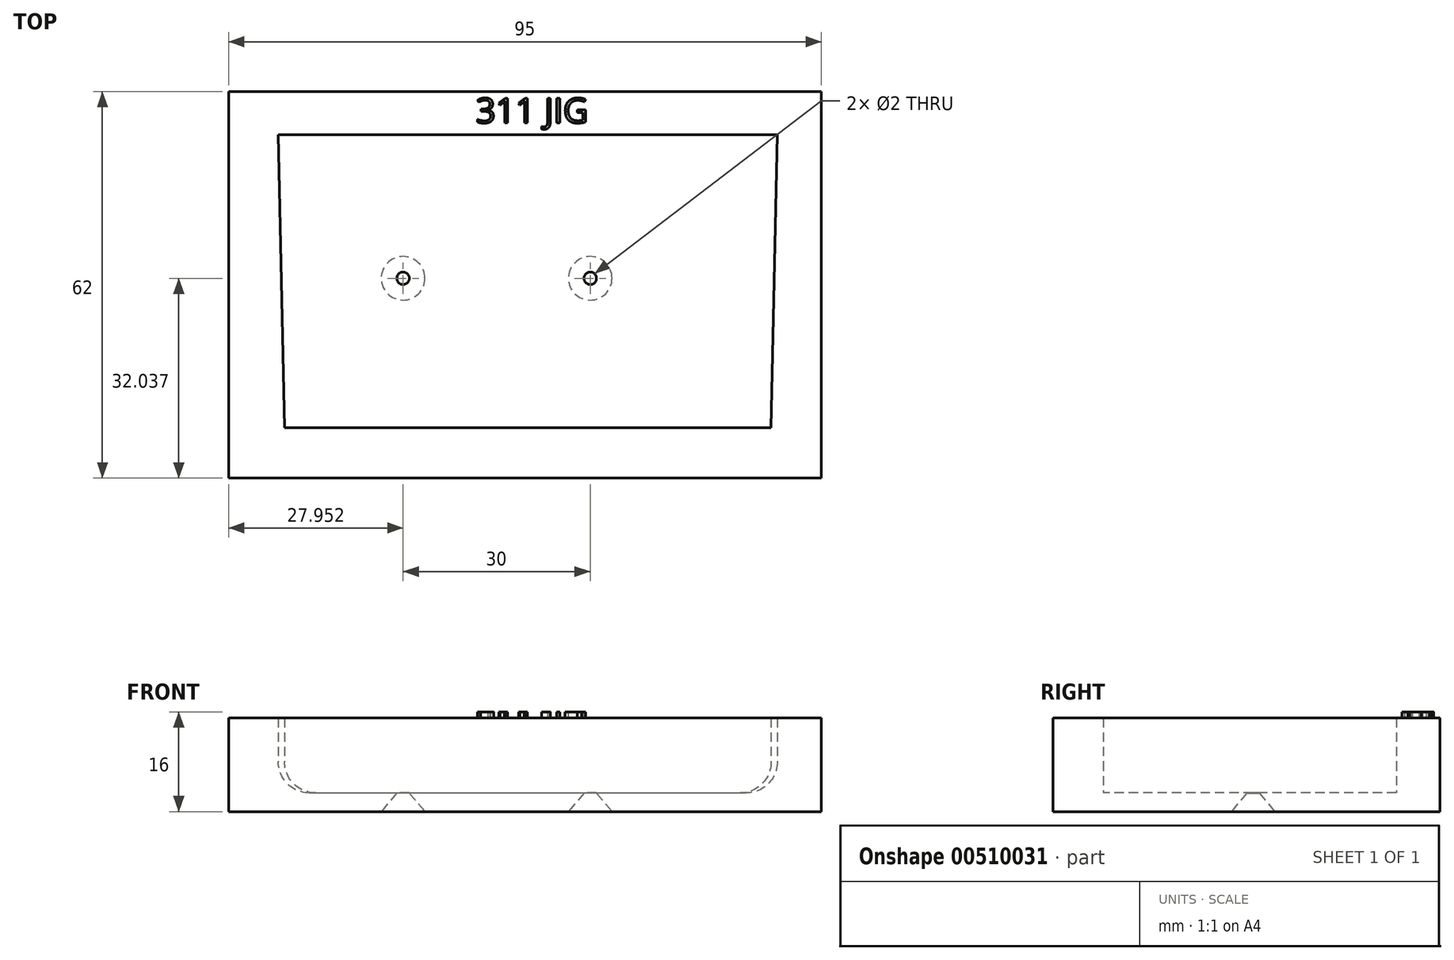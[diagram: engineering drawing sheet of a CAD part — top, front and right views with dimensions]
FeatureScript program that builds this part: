
annotation { "Feature Type Name" : "Feature", "Feature Type Description" : "" }
export const myFeature = defineFeature(function(context is Context, id is Id, definition is map)
    precondition{}
    {
        {
            var Q0;
            Q0=qCreatedBy(makeId("Top.planeOp"),FACE);
            var sketch = newSketch(context, id + "F0", { "sketchPlane" : qUnion([Q0])});
            skLineSegment(sketch, "E0.bottom", {"start": v(-47.5, 31) * mm, "end": v(47.5, 31) * mm});
            skLineSegment(sketch, "E0.top", {"start": v(-47.5, -31) * mm, "end": v(47.5, -31) * mm});
            skLineSegment(sketch, "E0.left", {"start": v(-47.5, 31) * mm, "end": v(-47.5, -31) * mm});
            skLineSegment(sketch, "E0.right", {"start": v(47.5, 31) * mm, "end": v(47.5, -31) * mm});
            skPoint(sketch, "E0.middle", {"position": v(0, 0) * mm});
            skSolve(sketch);
        }
        {
            var Q0;
            Q0=makeQuery(id+"F0.imprint","IMPRINT",FACE,{"disambiguationData":[TD([[makeQuery(id+"F0.imprint","IMPRINT",EDGE,{"derivedFrom":sQuery(id+"F0.wireOp",EDGE,"E0.bottom")}),-1.0]])]});
            var sketch = newSketch(context, id + "F1", { "sketchPlane" : qUnion([Q0])});
            skLineSegment(sketch, "E1", {"start": v(-39.55, 24.04) * mm, "end": v(40.45, 24.04) * mm});
            skLineSegment(sketch, "E2", {"start": v(-38.55, -22.95) * mm, "end": v(39.45, -22.95) * mm});
            skLineSegment(sketch, "E3", {"start": v(-39.55, 24.04) * mm, "end": v(-38.55, -22.95) * mm});
            skLineSegment(sketch, "E4", {"start": v(40.45, 24.04) * mm, "end": v(39.45, -22.95) * mm});
            skPoint(sketch, "E5.visualSharp", {"position": v(-38.55, -22.95) * mm});
            skLineSegment(sketch, "E5.filletArc", {"start": v(-38.55, -22.95) * mm, "end": v(-38.55, -22.95) * mm});
            skPoint(sketch, "E6.visualSharp", {"position": v(39.45, -22.95) * mm});
            skLineSegment(sketch, "E6.filletArc", {"start": v(39.45, -22.95) * mm, "end": v(39.45, -22.95) * mm});
            skSolve(sketch);
        }
        {
            var Q0;
            Q0=makeQuery(id+"F1.imprint","IMPRINT",FACE,{"disambiguationData":[TD([[makeQuery(id+"F1.imprint","IMPRINT",EDGE,{"derivedFrom":sQuery(id+"F1.wireOp",EDGE,"E1")}),1.0]])]});
            extrude(context, id + "F2", {"entities" : qUnion([Q0]), "depth" : 15 * mm});
        }
        {
            var Q0;
            Q0=makeQuery(id+"F0.imprint","IMPRINT",FACE,{"disambiguationData":[TD([[makeQuery(id+"F0.imprint","IMPRINT",EDGE,{"derivedFrom":sQuery(id+"F0.wireOp",EDGE,"E0.bottom")}),-1.0]])]});
            extrude(context, id + "F3", {"entities" : qUnion([Q0]), "operationType" : NewBodyOperationType.ADD, "depth" : 3 * mm});
        }
        {
            var Q0;
            Q0=qCreatedBy(makeId("Top.planeOp"),FACE);
            var sketch = newSketch(context, id + "F4", { "sketchPlane" : qUnion([Q0])});
            skPoint(sketch, "E7", {"position": v(-19.55, 1.04) * mm});
            skPoint(sketch, "E8", {"position": v(10.45, 1.04) * mm});
            skSolve(sketch);
        }
        {
            var Q0;
            Q0=sQuery(id+"F4.wireOp",VERTEX,"E8");
            var Q1;
            Q1=sQuery(id+"F4.wireOp",VERTEX,"E7");
            var Q2;
            Q2=makeQuery(id+"F2.opExtrude","SWEPT_BODY",BODY,{"disambiguationData":[OSD([sQuery(id+"F0.wireOp",EDGE,"E0.bottom"),sQuery(id+"F0.wireOp",EDGE,"E0.top"),sQuery(id+"F0.wireOp",EDGE,"E0.left"),sQuery(id+"F0.wireOp",EDGE,"E0.right"),sQuery(id+"F1.wireOp",EDGE,"E1"),sQuery(id+"F1.wireOp",EDGE,"E2"),sQuery(id+"F1.wireOp",EDGE,"E3"),sQuery(id+"F1.wireOp",EDGE,"E4")])]});
            hole(context, id + "F5", {"style" : HoleStyle.C_SINK, "endStyle" : HoleEndStyle.THROUGH, "oppositeDirection" : true, "holeDiameter" : 2 * mm, "cSinkDiameter" : 7 * mm, "cSinkAngle" : 80 * degree, "isTappedThrough" : true, "tappedDepth" : 12 * mm, "tapClearance" : 3, "locations" : qUnion([Q0, Q1]), "scope" : qUnion([Q2]), "startStyle" : HoleStartStyle.PART});
        }
        {
            var Q0;
            Q0=makeQuery(id+"F3.boolean.opBoolean","INTERSECT",EDGE,{"derivedFrom":[makeQuery(id+"F2.opExtrude","SWEPT_FACE",FACE,{"disambiguationData":[OSD([sQuery(id+"F1.wireOp",EDGE,"E3")])]}),makeQuery(id+"F3.opExtrude","CAP_FACE",FACE,{"disambiguationData":[OSD([sQuery(id+"F0.wireOp",EDGE,"E0.bottom"),sQuery(id+"F0.wireOp",EDGE,"E0.top"),sQuery(id+"F0.wireOp",EDGE,"E0.left"),sQuery(id+"F0.wireOp",EDGE,"E0.right")])],"isStart":false})]});
            fillet(context, id + "F6", {"entities" : qUnion([Q0]), "radius" : 5 * mm, "tangentPropagation" : true, "allowEdgeOverflow" : false});
        }
        {
            var Q0;
            Q0=makeQuery(id+"F3.boolean.opBoolean","INTERSECT",EDGE,{"derivedFrom":[makeQuery(id+"F2.opExtrude","SWEPT_FACE",FACE,{"disambiguationData":[OSD([sQuery(id+"F1.wireOp",EDGE,"E4")])]}),makeQuery(id+"F3.opExtrude","CAP_FACE",FACE,{"disambiguationData":[OSD([sQuery(id+"F0.wireOp",EDGE,"E0.bottom"),sQuery(id+"F0.wireOp",EDGE,"E0.top"),sQuery(id+"F0.wireOp",EDGE,"E0.left"),sQuery(id+"F0.wireOp",EDGE,"E0.right")])],"isStart":false})]});
            fillet(context, id + "F7", {"entities" : qUnion([Q0]), "radius" : 5 * mm, "tangentPropagation" : true, "allowEdgeOverflow" : false});
        }
        {
            var Q0;
            Q0=makeQuery(id+"F2.opExtrude","CAP_FACE",FACE,{"disambiguationData":[OSD([sQuery(id+"F0.wireOp",EDGE,"E0.bottom"),sQuery(id+"F0.wireOp",EDGE,"E0.top"),sQuery(id+"F0.wireOp",EDGE,"E0.left"),sQuery(id+"F0.wireOp",EDGE,"E0.right"),sQuery(id+"F1.wireOp",EDGE,"E1"),sQuery(id+"F1.wireOp",EDGE,"E2"),sQuery(id+"F1.wireOp",EDGE,"E3"),sQuery(id+"F1.wireOp",EDGE,"E4")])],"isStart":false});
            var sketch = newSketch(context, id + "F8", { "sketchPlane" : qUnion([Q0])});
            skText(sketch, "E9", { "text": "311 JIG", "fontName": "OpenSans-Regular.ttf"});
            const initialGuessF8  = {"E9": [-0.0079, 0.02596, 1, 0, 0.004]};
            skSetInitialGuess(sketch, initialGuessF8);
            skSolve(sketch);
        }
        {
            var Q0;
            Q0=qSketchRegion(id+"F8",true);
            extrude(context, id + "F9", {"entities" : qUnion([Q0]), "operationType" : NewBodyOperationType.ADD, "depth" : 1 * mm});
        }
    });
